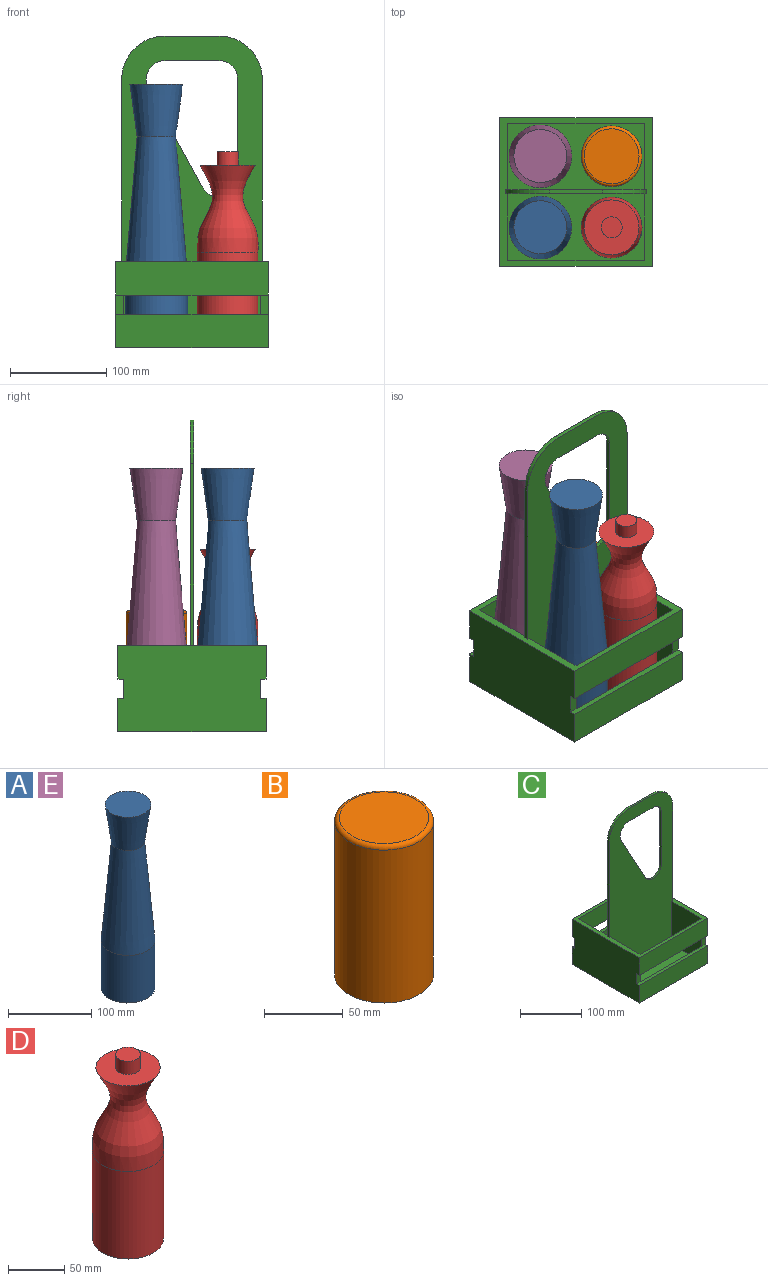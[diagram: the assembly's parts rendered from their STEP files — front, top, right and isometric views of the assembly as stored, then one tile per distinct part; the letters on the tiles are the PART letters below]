
ASSEMBLY  parts=5 mates=4
PART A: 5 faces, bbox 65x65x270 mm
  f0: cylinder r=32.5mm len=70mm, axis (0,0,-1), area 14294.2mm2, adj f1,f4
  f1: plane 65x65mm, normal (0,0,-1), area 3318.3mm2, adj f0
  f2: plane 55x55mm, normal (0,0,1), area 2375.8mm2, adj f3
  f3: cone r=20mm half-angle=7.8deg, axis (0,0,1), area 8200.1mm2, adj f2,f4
  f4: cone r=32.5mm half-angle=4.9deg, axis (0,0,-1), area 24096.6mm2, adj f0,f3
PART B: 4 faces, bbox 68.2x68.2x122.1 mm
  f0: plane 57x57mm, normal (0,0,1), area 2551.8mm2, adj f1
  f1: torus R=28.5mm, axis (0,0,1), area 900.4mm2, adj f0,f2
  f2: cylinder r=31.5mm len=119.09mm, axis (0,0,1), area 23570.4mm2, adj f1,f3
  f3: plane 63x63mm, normal (0,0,-1), area 3117.2mm2, adj f2
PART C: 39 faces, bbox 158x154x324 mm
  f0: plane 20x8mm, normal (0,-1,0), area 160mm2, adj f24,f26,f33,f37
  f1: plane 20x8mm, normal (0,-1,0), area 160mm2, adj f22,f23,f33,f37
  f2: plane 20x8mm, normal (0,1,0), area 160mm2, adj f20,f22,f28,f30
  f3: plane 20x8mm, normal (0,1,0), area 160mm2, adj f25,f26,f28,f30
  f4: plane 142x69mm, normal (0,0,1), area 9798mm2, adj f19,f20,f25,f32
  f5: plane 142x69mm, normal (0,0,1), area 9798mm2, adj f18,f23,f24,f35
  f6: plane 158x154mm, normal (0,0,-1), area 24332mm2, adj f22,f26,f31,f34
  f7: cylinder r=19.5mm len=19.5mm, axis (0,1,0), area 122.5mm2, adj f8,f17,f18,f19
  f8: plane 103.5x4mm, normal (-1,0,0), area 414mm2, adj f7,f9,f18,f19
  f9: cylinder r=19.5mm len=37.03mm, axis (0,1,0), area 207.1mm2, adj f8,f10,f18,f19
  f10: plane 102.8x56mm, normal (0.88,0,0.48), area 468.3mm2, adj f9,f11,f18,f19
  f11: cylinder r=19.5mm len=28.06mm, axis (0,1,0), area 158mm2, adj f10,f17,f18,f19
  f12: plane 189x4mm, normal (-1,0,0), area 756mm2, adj f16,f18,f19,f21
  f13: plane 189x4mm, normal (1,0,0), area 756mm2, adj f14,f18,f19,f21
  f14: cylinder r=45mm len=45mm, axis (0,1,0), area 282.7mm2, adj f13,f15,f18,f19
  f15: plane 56x4mm, normal (0,0,1), area 224mm2, adj f14,f16,f18,f19
  f16: cylinder r=45mm len=45mm, axis (0,1,0), area 282.7mm2, adj f12,f15,f18,f19
  f17: plane 56x4mm, normal (0,0,-1), area 224mm2, adj f7,f11,f18,f19
  f18: plane 320x146mm, normal (0,-1,0), area 36055.1mm2, adj f5,f7,f8,f9,f10,f11,f12,f13
  f19: plane 320x146mm, normal (0,1,0), area 36055.1mm2, adj f4,f7,f8,f9,f10,f11,f12,f13
  f20: plane 86x69mm, normal (-1,0,0), area 5934mm2, adj f2,f4,f19,f21,f27,f32
  f21: plane 158x154mm, normal (0,0,1), area 4152mm2, adj f12,f13,f18,f19,f20,f22,f23,f24
  f22: plane 154x90mm, normal (1,0,0), area 13620mm2, adj f1,f2,f6,f21,f28,f29,f30,f31
  f23: plane 86x69mm, normal (-1,0,0), area 5934mm2, adj f1,f5,f18,f21,f35,f36
  f24: plane 86x69mm, normal (1,0,0), area 5934mm2, adj f0,f5,f18,f21,f35,f36
  f25: plane 86x69mm, normal (1,0,0), area 5934mm2, adj f3,f4,f19,f21,f27,f32
  f26: plane 154x90mm, normal (-1,0,0), area 13620mm2, adj f0,f3,f6,f21,f28,f29,f30,f31
  f27: plane 142x35mm, normal (0,-1,0), area 4970mm2, adj f20,f21,f25,f28
  f28: plane 158x6mm, normal (0,0,-1), area 948mm2, adj f2,f3,f22,f26,f27,f29
  f29: plane 158x35mm, normal (0,1,0), area 5530mm2, adj f21,f22,f26,f28
  f30: plane 158x6mm, normal (0,0,1), area 948mm2, adj f2,f3,f22,f26,f31,f32
  f31: plane 158x35mm, normal (0,1,0), area 5530mm2, adj f6,f22,f26,f30
  f32: plane 142x31mm, normal (0,-1,0), area 4402mm2, adj f4,f20,f25,f30
  f33: plane 158x6mm, normal (0,0,1), area 948mm2, adj f0,f1,f22,f26,f34,f35
  f34: plane 158x35mm, normal (0,-1,0), area 5530mm2, adj f6,f22,f26,f33
  f35: plane 142x31mm, normal (0,1,0), area 4402mm2, adj f5,f23,f24,f33
  f36: plane 142x35mm, normal (0,1,0), area 4970mm2, adj f21,f23,f24,f37
  f37: plane 158x6mm, normal (0,0,-1), area 948mm2, adj f0,f1,f22,f26,f36,f38
  f38: plane 158x35mm, normal (0,-1,0), area 5530mm2, adj f21,f22,f26,f37
PART D: 6 faces, bbox 63.4x63.4x200 mm
  f0: plane 22x22mm, normal (0,0,1), area 380.1mm2, adj f1
  f1: cylinder r=11mm len=22mm, axis (0,0,1), area 987.6mm2, adj f0,f2
  f2: plane 57x57mm, normal (0,0,1), area 2171.6mm2, adj f1,f3
  f3: revolved ~90.72x63.36mm, area 14401.1mm2, adj f2,f4
  f4: cylinder r=31.5mm len=95mm, axis (0,0,1), area 18802.4mm2, adj f3,f5
  f5: plane 63x63mm, normal (0,0,-1), area 3117.2mm2, adj f4
PART E: same geometry as A
PLACE A t=(-122.06,27.98,17.95)mm
PLACE B t=(-48.06,101.98,17.95)mm
PLACE C t=(-85.06,64.98,13.95)mm
PLACE D t=(-48.06,27.98,17.95)mm
PLACE E t=(-122.06,101.98,17.95)mm
MATE fastened A.f4 <-> C.f5  axis (0,0,-1) through (-122.06,27.98,17.95)mm
MATE fastened B.f1 <-> C.f4  axis (0,0,-1) through (-48.06,101.98,17.95)mm
MATE fastened D.f1 <-> C.f5  axis (0,0,-1) through (-48.06,27.98,17.95)mm
MATE fastened E.f4 <-> C.f4  axis (0,0,-1) through (-122.06,101.98,17.95)mm
